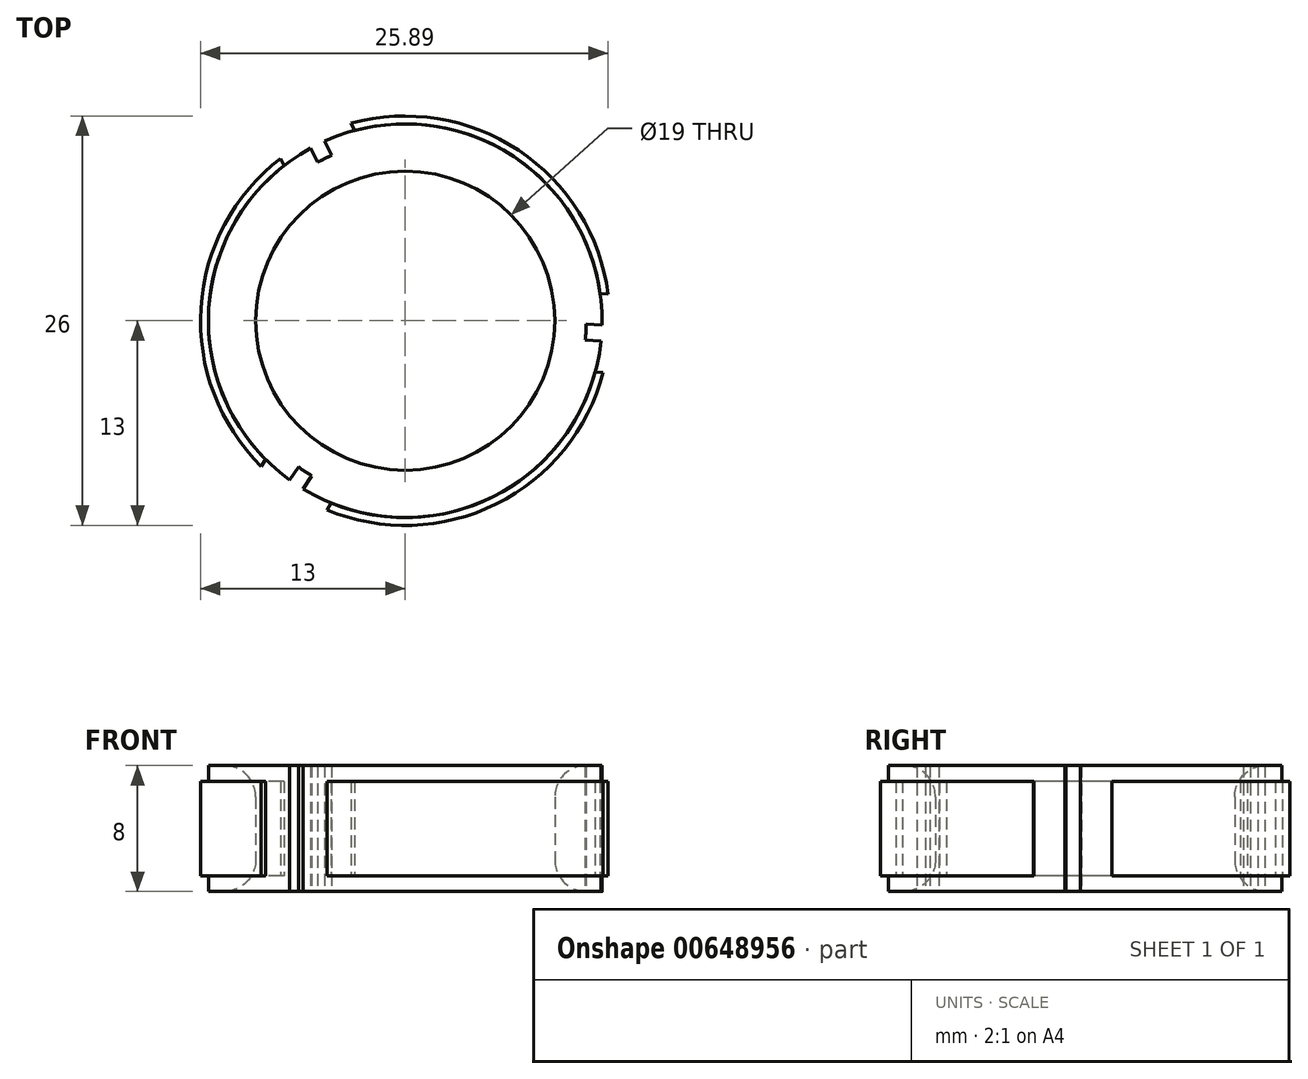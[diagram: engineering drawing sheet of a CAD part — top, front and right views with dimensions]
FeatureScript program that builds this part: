
annotation { "Feature Type Name" : "Feature", "Feature Type Description" : "" }
export const myFeature = defineFeature(function(context is Context, id is Id, definition is map)
    precondition{}
    {
        {
            var Q0;
            Q0=qCreatedBy(makeId("Top.planeOp"),FACE);
            var sketch = newSketch(context, id + "F0", { "sketchPlane" : qUnion([Q0])});
            skCircle(sketch, "E0", {"center": v(0, 0) * mm, "radius": 9.5 * mm});
            skCircle(sketch, "E1", {"center": v(0, 0) * mm, "radius": 11.5 * mm});
            skLineSegment(sketch, "E2", {"start": v(0, 0) * mm, "end": v(-10.32, -15.53) * mm});
            skLineSegment(sketch, "E3", {"start": v(0, 0) * mm, "end": v(20.96, -1.32) * mm});
            skLineSegment(sketch, "E4", {"start": v(0, 0) * mm, "end": v(-8.8, 17.7) * mm});
            skLineSegment(sketch, "E5", {"start": v(-8.4, 18.03) * mm, "end": v(-2.41, 5.99) * mm});
            skLineSegment(sketch, "E6", {"start": v(-8.01, 15.01) * mm, "end": v(-3.78, 6.5) * mm});
            skLineSegment(sketch, "E7", {"start": v(-4.43, -5.77) * mm, "end": v(-9.06, -12.74) * mm});
            skLineSegment(sketch, "E8", {"start": v(-4.56, -7.77) * mm, "end": v(-8.54, -13.76) * mm});
            skPoint(sketch, "E8.startSnap0", {"position": v(-5.16, -7.77) * mm});
            skLineSegment(sketch, "E9", {"start": v(7.97, 0) * mm, "end": v(15.23, -0.46) * mm});
            skLineSegment(sketch, "E10", {"start": v(6.7, -0.92) * mm, "end": v(14.71, -1.43) * mm});
            skCircle(sketch, "E11", {"center": v(0, 0) * mm, "radius": 12.5 * mm});
            skLineSegment(sketch, "E12", {"start": v(-2.5, -8.27) * mm, "end": v(-5.94, -13.46) * mm});
            skLineSegment(sketch, "E13", {"start": v(-6.43, -5.17) * mm, "end": v(-10.65, -11.52) * mm});
            skLineSegment(sketch, "E14", {"start": v(-5.55, 5.56) * mm, "end": v(-8.6, 11.69) * mm});
            skLineSegment(sketch, "E15", {"start": v(-1.17, 7.97) * mm, "end": v(-3.88, 13.44) * mm});
            skLineSegment(sketch, "E16", {"start": v(8.89, 1.95) * mm, "end": v(14.7, 1.58) * mm});
            skLineSegment(sketch, "E17", {"start": v(7.83, -3) * mm, "end": v(14.83, -3.44) * mm});
            skCircle(sketch, "E18", {"center": v(0, 0) * mm, "radius": 13 * mm});
            skSolve(sketch);
        }
        {
            var Q0;
            Q0=makeQuery(id+"F0.imprint","IMPRINT",FACE,{"disambiguationData":[TD([[makeQuery(id+"F0.imprint","IMPRINT",EDGE,{"derivedFrom":sQuery(id+"F0.wireOp",EDGE,"E0")}),-1.0]])]});
            var Q1;
            {var subQ0=sQuery(id+"F0.wireOp",EDGE,"E5");var subQ1=sQuery(id+"F0.wireOp",EDGE,"E1");var subQ2=makeQuery(id+"F0.imprint","INTERSECT",VERTEX,{"derivedFrom":[subQ1,subQ0]});Q1=makeQuery(id+"F0.imprint","IMPRINT",FACE,{"disambiguationData":[TD([[makeQuery(id+"F0.imprint","IMPRINT",EDGE,{"disambiguationData":[TD([[subQ2,1.0]])],"derivedFrom":subQ1}),-1.0]])]});}
            var Q2;
            {var subQ0=sQuery(id+"F0.wireOp",EDGE,"E6");var subQ1=sQuery(id+"F0.wireOp",EDGE,"E1");var subQ2=makeQuery(id+"F0.imprint","INTERSECT",VERTEX,{"derivedFrom":[subQ1,subQ0]});Q2=makeQuery(id+"F0.imprint","IMPRINT",FACE,{"disambiguationData":[TD([[makeQuery(id+"F0.imprint","IMPRINT",EDGE,{"disambiguationData":[TD([[subQ2,-1.0]])],"derivedFrom":subQ1}),-1.0]])]});}
            var Q3;
            {var subQ0=sQuery(id+"F0.wireOp",EDGE,"E8");var subQ1=sQuery(id+"F0.wireOp",EDGE,"E1");var subQ2=makeQuery(id+"F0.imprint","INTERSECT",VERTEX,{"derivedFrom":[subQ1,subQ0]});Q3=makeQuery(id+"F0.imprint","IMPRINT",FACE,{"disambiguationData":[TD([[makeQuery(id+"F0.imprint","IMPRINT",EDGE,{"disambiguationData":[TD([[subQ2,-1.0]])],"derivedFrom":subQ1}),-1.0]])]});}
            var Q4;
            {var subQ0=sQuery(id+"F0.wireOp",EDGE,"E12");var subQ1=sQuery(id+"F0.wireOp",EDGE,"E1");var subQ2=makeQuery(id+"F0.imprint","INTERSECT",VERTEX,{"derivedFrom":[subQ1,subQ0]});Q4=makeQuery(id+"F0.imprint","IMPRINT",FACE,{"disambiguationData":[TD([[makeQuery(id+"F0.imprint","IMPRINT",EDGE,{"disambiguationData":[TD([[subQ2,-1.0]])],"derivedFrom":subQ1}),-1.0]])]});}
            var Q5;
            {var subQ0=sQuery(id+"F0.wireOp",EDGE,"E13");var subQ1=sQuery(id+"F0.wireOp",EDGE,"E1");var subQ2=makeQuery(id+"F0.imprint","INTERSECT",VERTEX,{"derivedFrom":[subQ1,subQ0]});Q5=makeQuery(id+"F0.imprint","IMPRINT",FACE,{"disambiguationData":[TD([[makeQuery(id+"F0.imprint","IMPRINT",EDGE,{"disambiguationData":[TD([[subQ2,-1.0]])],"derivedFrom":subQ1}),-1.0]])]});}
            var Q6;
            {var subQ0=sQuery(id+"F0.wireOp",EDGE,"E14");var subQ1=sQuery(id+"F0.wireOp",EDGE,"E1");var subQ2=makeQuery(id+"F0.imprint","INTERSECT",VERTEX,{"derivedFrom":[subQ1,subQ0]});Q6=makeQuery(id+"F0.imprint","IMPRINT",FACE,{"disambiguationData":[TD([[makeQuery(id+"F0.imprint","IMPRINT",EDGE,{"disambiguationData":[TD([[subQ2,-1.0]])],"derivedFrom":subQ1}),-1.0]])]});}
            var Q7;
            {var subQ0=sQuery(id+"F0.wireOp",EDGE,"E15");var subQ1=sQuery(id+"F0.wireOp",EDGE,"E1");var subQ2=makeQuery(id+"F0.imprint","INTERSECT",VERTEX,{"derivedFrom":[subQ1,subQ0]});Q7=makeQuery(id+"F0.imprint","IMPRINT",FACE,{"disambiguationData":[TD([[makeQuery(id+"F0.imprint","IMPRINT",EDGE,{"disambiguationData":[TD([[subQ2,1.0]])],"derivedFrom":subQ1}),-1.0]])]});}
            var Q8;
            {var subQ0=sQuery(id+"F0.wireOp",EDGE,"E16");var subQ1=sQuery(id+"F0.wireOp",EDGE,"E1");var subQ2=makeQuery(id+"F0.imprint","INTERSECT",VERTEX,{"derivedFrom":[subQ1,subQ0]});Q8=makeQuery(id+"F0.imprint","IMPRINT",FACE,{"disambiguationData":[TD([[makeQuery(id+"F0.imprint","IMPRINT",EDGE,{"disambiguationData":[TD([[subQ2,1.0]])],"derivedFrom":subQ1}),-1.0]])]});}
            var Q9;
            {var subQ0=sQuery(id+"F0.wireOp",EDGE,"E17");var subQ1=sQuery(id+"F0.wireOp",EDGE,"E1");var subQ2=makeQuery(id+"F0.imprint","INTERSECT",VERTEX,{"derivedFrom":[subQ1,subQ0]});Q9=makeQuery(id+"F0.imprint","IMPRINT",FACE,{"disambiguationData":[TD([[makeQuery(id+"F0.imprint","IMPRINT",EDGE,{"disambiguationData":[TD([[subQ2,-1.0]])],"derivedFrom":subQ1}),-1.0]])]});}
            var Q10;
            {var subQ0=sQuery(id+"F0.wireOp",EDGE,"E12");var subQ1=sQuery(id+"F0.wireOp",EDGE,"E11");var subQ2=makeQuery(id+"F0.imprint","INTERSECT",VERTEX,{"derivedFrom":[subQ1,subQ0]});Q10=makeQuery(id+"F0.imprint","IMPRINT",FACE,{"disambiguationData":[TD([[makeQuery(id+"F0.imprint","IMPRINT",EDGE,{"disambiguationData":[TD([[subQ2,-1.0]])],"derivedFrom":subQ1}),-1.0]])]});}
            var Q11;
            {var subQ0=sQuery(id+"F0.wireOp",EDGE,"E14");var subQ1=sQuery(id+"F0.wireOp",EDGE,"E11");var subQ2=makeQuery(id+"F0.imprint","INTERSECT",VERTEX,{"derivedFrom":[subQ1,subQ0]});Q11=makeQuery(id+"F0.imprint","IMPRINT",FACE,{"disambiguationData":[TD([[makeQuery(id+"F0.imprint","IMPRINT",EDGE,{"disambiguationData":[TD([[subQ2,-1.0]])],"derivedFrom":subQ1}),-1.0]])]});}
            var Q12;
            {var subQ0=sQuery(id+"F0.wireOp",EDGE,"E15");var subQ1=sQuery(id+"F0.wireOp",EDGE,"E11");var subQ2=makeQuery(id+"F0.imprint","INTERSECT",VERTEX,{"derivedFrom":[subQ1,subQ0]});Q12=makeQuery(id+"F0.imprint","IMPRINT",FACE,{"disambiguationData":[TD([[makeQuery(id+"F0.imprint","IMPRINT",EDGE,{"disambiguationData":[TD([[subQ2,1.0]])],"derivedFrom":subQ1}),-1.0]])]});}
            extrude(context, id + "F1", {"entities" : qUnion([Q0, Q1, Q2, Q3, Q4, Q5, Q6, Q7, Q8, Q9, Q10, Q11, Q12]), "depth" : 8 * mm, "offsetDistance" : 25 * mm});
        }
        {
            var Q0;
            {var subQ0=sQuery(id+"F0.wireOp",EDGE,"E12");var subQ1=sQuery(id+"F0.wireOp",EDGE,"E11");var subQ2=makeQuery(id+"F0.imprint","INTERSECT",VERTEX,{"derivedFrom":[subQ1,subQ0]});Q0=makeQuery(id+"F0.imprint","IMPRINT",FACE,{"disambiguationData":[TD([[makeQuery(id+"F0.imprint","IMPRINT",EDGE,{"disambiguationData":[TD([[subQ2,-1.0]])],"derivedFrom":subQ1}),-1.0]])]});}
            var Q1;
            {var subQ0=sQuery(id+"F0.wireOp",EDGE,"E15");var subQ1=sQuery(id+"F0.wireOp",EDGE,"E11");var subQ2=makeQuery(id+"F0.imprint","INTERSECT",VERTEX,{"derivedFrom":[subQ1,subQ0]});Q1=makeQuery(id+"F0.imprint","IMPRINT",FACE,{"disambiguationData":[TD([[makeQuery(id+"F0.imprint","IMPRINT",EDGE,{"disambiguationData":[TD([[subQ2,1.0]])],"derivedFrom":subQ1}),-1.0]])]});}
            var Q2;
            {var subQ0=sQuery(id+"F0.wireOp",EDGE,"E14");var subQ1=sQuery(id+"F0.wireOp",EDGE,"E11");var subQ2=makeQuery(id+"F0.imprint","INTERSECT",VERTEX,{"derivedFrom":[subQ1,subQ0]});Q2=makeQuery(id+"F0.imprint","IMPRINT",FACE,{"disambiguationData":[TD([[makeQuery(id+"F0.imprint","IMPRINT",EDGE,{"disambiguationData":[TD([[subQ2,-1.0]])],"derivedFrom":subQ1}),-1.0]])]});}
            extrude(context, id + "F2", {"entities" : qUnion([Q0, Q1, Q2]), "operationType" : NewBodyOperationType.REMOVE, "oppositeDirection" : true, "depth" : -1 * mm, "offsetDistance" : 25 * mm});
        }
        {
            var Q0;
            {var subQ0=sQuery(id+"F0.wireOp",EDGE,"E12");var subQ1=sQuery(id+"F0.wireOp",EDGE,"E11");var subQ2=makeQuery(id+"F0.imprint","INTERSECT",VERTEX,{"derivedFrom":[subQ1,subQ0]});Q0=makeQuery(id+"F0.imprint","IMPRINT",FACE,{"disambiguationData":[TD([[makeQuery(id+"F0.imprint","IMPRINT",EDGE,{"disambiguationData":[TD([[subQ2,-1.0]])],"derivedFrom":subQ1}),-1.0]])]});}
            var Q1;
            {var subQ0=sQuery(id+"F0.wireOp",EDGE,"E14");var subQ1=sQuery(id+"F0.wireOp",EDGE,"E11");var subQ2=makeQuery(id+"F0.imprint","INTERSECT",VERTEX,{"derivedFrom":[subQ1,subQ0]});Q1=makeQuery(id+"F0.imprint","IMPRINT",FACE,{"disambiguationData":[TD([[makeQuery(id+"F0.imprint","IMPRINT",EDGE,{"disambiguationData":[TD([[subQ2,-1.0]])],"derivedFrom":subQ1}),-1.0]])]});}
            var Q2;
            {var subQ0=sQuery(id+"F0.wireOp",EDGE,"E15");var subQ1=sQuery(id+"F0.wireOp",EDGE,"E11");var subQ2=makeQuery(id+"F0.imprint","INTERSECT",VERTEX,{"derivedFrom":[subQ1,subQ0]});Q2=makeQuery(id+"F0.imprint","IMPRINT",FACE,{"disambiguationData":[TD([[makeQuery(id+"F0.imprint","IMPRINT",EDGE,{"disambiguationData":[TD([[subQ2,1.0]])],"derivedFrom":subQ1}),-1.0]])]});}
            extrude(context, id + "F3", {"entities" : qUnion([Q0, Q1, Q2]), "operationType" : NewBodyOperationType.REMOVE, "depth" : 8 * mm, "offsetDistance" : 25 * mm, "hasSecondDirection" : true, "secondDirectionOppositeDirection" : false, "secondDirectionDepth" : 7 * mm});
        }
        {
            var Q0;
            Q0=makeQuery(id+"F1.opExtrude","CAP_EDGE",EDGE,{"disambiguationData":[OSD([sQuery(id+"F0.wireOp",EDGE,"E0")])],"isStart":false});
            var Q1;
            Q1=makeQuery(id+"F1.opExtrude","CAP_EDGE",EDGE,{"disambiguationData":[OSD([sQuery(id+"F0.wireOp",EDGE,"E0")])],"isStart":true});
            fillet(context, id + "F4", {"entities" : qUnion([Q0, Q1]), "radius" : 2 * mm, "tangentPropagation" : true, "allowEdgeOverflow" : false});
        }
    });
